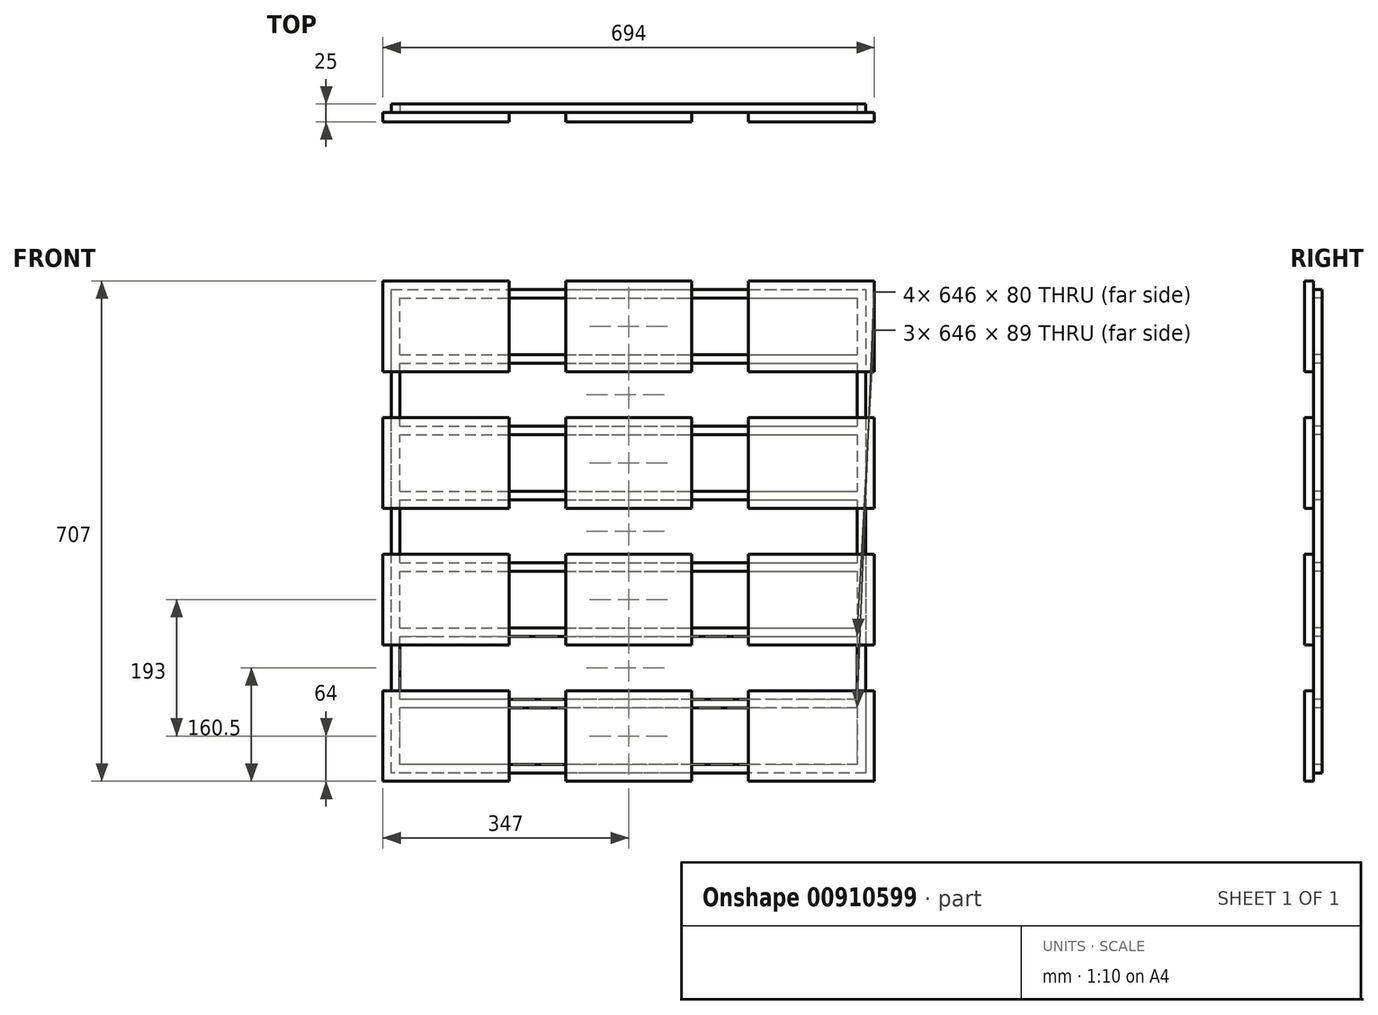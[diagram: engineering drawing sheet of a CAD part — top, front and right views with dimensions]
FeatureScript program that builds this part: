
annotation { "Feature Type Name" : "Feature", "Feature Type Description" : "" }
export const myFeature = defineFeature(function(context is Context, id is Id, definition is map)
    precondition{}
    {
        {
            var Q0;
            Q0=qCreatedBy(makeId("Front.planeOp"),FACE);
            var sketch = newSketch(context, id + "F0", { "sketchPlane" : qUnion([Q0])});
            skLineSegment(sketch, "E0", {"start": v(0, 0) * mm, "end": v(694, 0) * mm, "construction": true});
            skLineSegment(sketch, "E1", {"start": v(694, 0) * mm, "end": v(694, -707) * mm, "construction": true});
            skLineSegment(sketch, "E2", {"start": v(694, -707) * mm, "end": v(0, -707) * mm, "construction": true});
            skLineSegment(sketch, "E3", {"start": v(0, -707) * mm, "end": v(0, 0) * mm, "construction": true});
            skLineSegment(sketch, "E4.0", {"start": v(24, -24) * mm, "end": v(670, -24) * mm});
            skLineSegment(sketch, "E4.1", {"start": v(24, -683) * mm, "end": v(24, -603) * mm});
            skLineSegment(sketch, "E4.2", {"start": v(670, -683) * mm, "end": v(24, -683) * mm});
            skLineSegment(sketch, "E4.3", {"start": v(670, -24) * mm, "end": v(670, -104) * mm});
            skLineSegment(sketch, "E5", {"start": v(24, -116) * mm, "end": v(670, -116) * mm});
            skLineSegment(sketch, "E6", {"start": v(24, -205) * mm, "end": v(670, -205) * mm});
            skLineSegment(sketch, "E7", {"start": v(24, -309) * mm, "end": v(670, -309) * mm});
            skLineSegment(sketch, "E8", {"start": v(24, -398) * mm, "end": v(670, -398) * mm});
            skLineSegment(sketch, "E9.0", {"start": v(24, -104) * mm, "end": v(670, -104) * mm});
            skLineSegment(sketch, "E10.0", {"start": v(24, -217) * mm, "end": v(670, -217) * mm});
            skLineSegment(sketch, "E11.0", {"start": v(24, -410) * mm, "end": v(670, -410) * mm});
            skLineSegment(sketch, "E12.0", {"start": v(24, -297) * mm, "end": v(670, -297) * mm});
            skLineSegment(sketch, "E13.trimOffspring", {"start": v(670, -116) * mm, "end": v(670, -205) * mm});
            skLineSegment(sketch, "E14.trimOffspring", {"start": v(670, -217) * mm, "end": v(670, -297) * mm});
            skLineSegment(sketch, "E15.trimOffspring", {"start": v(670, -309) * mm, "end": v(670, -398) * mm});
            skLineSegment(sketch, "E16.trimOffspring", {"start": v(670, -410) * mm, "end": v(670, -490) * mm});
            skLineSegment(sketch, "E17.trimOffspring", {"start": v(24, -104) * mm, "end": v(24, -24) * mm});
            skLineSegment(sketch, "E18.trimOffspring", {"start": v(24, -205) * mm, "end": v(24, -116) * mm});
            skLineSegment(sketch, "E19.trimOffspring", {"start": v(24, -398) * mm, "end": v(24, -309) * mm});
            skLineSegment(sketch, "E20.trimOffspring", {"start": v(24, -297) * mm, "end": v(24, -217) * mm});
            skLineSegment(sketch, "E21.0", {"start": v(12, -695) * mm, "end": v(12, -12) * mm});
            skLineSegment(sketch, "E21.1", {"start": v(682, -695) * mm, "end": v(12, -695) * mm});
            skLineSegment(sketch, "E21.2", {"start": v(682, -12) * mm, "end": v(682, -695) * mm});
            skLineSegment(sketch, "E21.3", {"start": v(12, -12) * mm, "end": v(682, -12) * mm});
            skLineSegment(sketch, "E22", {"start": v(24, -490) * mm, "end": v(670, -490) * mm});
            skLineSegment(sketch, "E23", {"start": v(24, -502) * mm, "end": v(670, -502) * mm});
            skPoint(sketch, "E23.endSnap0", {"position": v(670, -546.5) * mm});
            skLineSegment(sketch, "E24", {"start": v(670, -591) * mm, "end": v(24, -591) * mm});
            skLineSegment(sketch, "E25", {"start": v(670, -603) * mm, "end": v(24, -603) * mm});
            skLineSegment(sketch, "E26.trimOffspring", {"start": v(24, -490) * mm, "end": v(24, -410) * mm});
            skLineSegment(sketch, "E27.trimOffspring", {"start": v(24, -591) * mm, "end": v(24, -502) * mm});
            skLineSegment(sketch, "E28.trimOffspring", {"start": v(670, -502) * mm, "end": v(670, -591) * mm});
            skLineSegment(sketch, "E29.trimOffspring", {"start": v(670, -603) * mm, "end": v(670, -683) * mm});
            skSolve(sketch);
        }
        {
            var Q0;
            Q0=makeQuery(id+"F0.imprint","IMPRINT",FACE,{"disambiguationData":[TD([[makeQuery(id+"F0.imprint","IMPRINT",EDGE,{"derivedFrom":sQuery(id+"F0.wireOp",EDGE,"E4.0")}),1.0]])]});
            extrude(context, id + "F1", {"entities" : qUnion([Q0]), "oppositeDirection" : true, "depth" : 12 * mm, "offsetDistance" : 25 * mm});
        }
        {
            var Q0;
            Q0=qCreatedBy(makeId("Front.planeOp"),FACE);
            var sketch = newSketch(context, id + "F2", { "sketchPlane" : qUnion([Q0])});
            skLineSegment(sketch, "E30.bottom", {"start": v(0, 0) * mm, "end": v(178, 0) * mm});
            skLineSegment(sketch, "E30.top", {"start": v(0, -128) * mm, "end": v(178, -128) * mm});
            skLineSegment(sketch, "E30.left", {"start": v(0, 0) * mm, "end": v(0, -128) * mm});
            skLineSegment(sketch, "E30.right", {"start": v(178, 0) * mm, "end": v(178, -128) * mm});
            skLineSegment(sketch, "E31.bottom", {"start": v(258, 0) * mm, "end": v(436, 0) * mm});
            skLineSegment(sketch, "E31.top", {"start": v(258, -128) * mm, "end": v(436, -128) * mm});
            skLineSegment(sketch, "E31.left", {"start": v(258, 0) * mm, "end": v(258, -128) * mm});
            skLineSegment(sketch, "E31.right", {"start": v(436, 0) * mm, "end": v(436, -128) * mm});
            skLineSegment(sketch, "E32.bottom", {"start": v(516, 0) * mm, "end": v(694, 0) * mm});
            skLineSegment(sketch, "E32.top", {"start": v(516, -128) * mm, "end": v(694, -128) * mm});
            skLineSegment(sketch, "E32.left", {"start": v(516, 0) * mm, "end": v(516, -128) * mm});
            skLineSegment(sketch, "E32.right", {"start": v(694, 0) * mm, "end": v(694, -128) * mm});
            skLineSegment(sketch, "E33.bottom", {"start": v(0, -193) * mm, "end": v(178, -193) * mm});
            skLineSegment(sketch, "E33.top", {"start": v(0, -321) * mm, "end": v(178, -321) * mm});
            skLineSegment(sketch, "E33.left", {"start": v(0, -193) * mm, "end": v(0, -321) * mm});
            skLineSegment(sketch, "E33.right", {"start": v(178, -193) * mm, "end": v(178, -321) * mm});
            skLineSegment(sketch, "E34.bottom", {"start": v(258, -193) * mm, "end": v(436, -193) * mm});
            skLineSegment(sketch, "E34.top", {"start": v(258, -321) * mm, "end": v(436, -321) * mm});
            skLineSegment(sketch, "E34.left", {"start": v(258, -193) * mm, "end": v(258, -321) * mm});
            skLineSegment(sketch, "E34.right", {"start": v(436, -193) * mm, "end": v(436, -321) * mm});
            skLineSegment(sketch, "E35.bottom", {"start": v(516, -193) * mm, "end": v(694, -193) * mm});
            skLineSegment(sketch, "E35.top", {"start": v(516, -321) * mm, "end": v(694, -321) * mm});
            skLineSegment(sketch, "E35.left", {"start": v(516, -193) * mm, "end": v(516, -321) * mm});
            skLineSegment(sketch, "E35.right", {"start": v(694, -193) * mm, "end": v(694, -321) * mm});
            skLineSegment(sketch, "E36.bottom", {"start": v(0, -386) * mm, "end": v(178, -386) * mm});
            skLineSegment(sketch, "E36.top", {"start": v(0, -514) * mm, "end": v(178, -514) * mm});
            skLineSegment(sketch, "E36.left", {"start": v(0, -386) * mm, "end": v(0, -514) * mm});
            skLineSegment(sketch, "E36.right", {"start": v(178, -386) * mm, "end": v(178, -514) * mm});
            skLineSegment(sketch, "E37.bottom", {"start": v(258, -386) * mm, "end": v(436, -386) * mm});
            skLineSegment(sketch, "E37.top", {"start": v(258, -514) * mm, "end": v(436, -514) * mm});
            skLineSegment(sketch, "E37.left", {"start": v(258, -386) * mm, "end": v(258, -514) * mm});
            skLineSegment(sketch, "E37.right", {"start": v(436, -386) * mm, "end": v(436, -514) * mm});
            skLineSegment(sketch, "E38.bottom", {"start": v(516, -386) * mm, "end": v(694, -386) * mm});
            skLineSegment(sketch, "E38.top", {"start": v(516, -514) * mm, "end": v(694, -514) * mm});
            skLineSegment(sketch, "E38.left", {"start": v(516, -386) * mm, "end": v(516, -514) * mm});
            skLineSegment(sketch, "E38.right", {"start": v(694, -386) * mm, "end": v(694, -514) * mm});
            skLineSegment(sketch, "E39", {"start": v(178, 0) * mm, "end": v(258, 0) * mm, "construction": true});
            skLineSegment(sketch, "E40", {"start": v(436, 0) * mm, "end": v(516, 0) * mm, "construction": true});
            skLineSegment(sketch, "E41", {"start": v(694, 0) * mm, "end": v(774, 0) * mm, "construction": true});
            skLineSegment(sketch, "E42", {"start": v(0, -128) * mm, "end": v(0, -193) * mm, "construction": true});
            skLineSegment(sketch, "E43", {"start": v(0, -321) * mm, "end": v(0, -386) * mm, "construction": true});
            skLineSegment(sketch, "E44.bottom", {"start": v(0, -579) * mm, "end": v(178, -579) * mm});
            skLineSegment(sketch, "E44.top", {"start": v(0, -707) * mm, "end": v(178, -707) * mm});
            skLineSegment(sketch, "E44.left", {"start": v(0, -579) * mm, "end": v(0, -707) * mm});
            skLineSegment(sketch, "E44.right", {"start": v(178, -579) * mm, "end": v(178, -707) * mm});
            skLineSegment(sketch, "E45.bottom", {"start": v(258, -579) * mm, "end": v(436, -579) * mm});
            skLineSegment(sketch, "E45.top", {"start": v(258, -707) * mm, "end": v(436, -707) * mm});
            skLineSegment(sketch, "E45.left", {"start": v(258, -579) * mm, "end": v(258, -707) * mm});
            skLineSegment(sketch, "E45.right", {"start": v(436, -579) * mm, "end": v(436, -707) * mm});
            skLineSegment(sketch, "E46.bottom", {"start": v(516, -579) * mm, "end": v(694, -579) * mm});
            skLineSegment(sketch, "E46.top", {"start": v(516, -707) * mm, "end": v(694, -707) * mm});
            skLineSegment(sketch, "E46.left", {"start": v(516, -579) * mm, "end": v(516, -707) * mm});
            skLineSegment(sketch, "E46.right", {"start": v(694, -579) * mm, "end": v(694, -707) * mm});
            skLineSegment(sketch, "E47", {"start": v(0, -514) * mm, "end": v(0, -579) * mm, "construction": true});
            skSolve(sketch);
        }
        {
            var Q0;
            Q0=qSketchRegion(id+"F2",true);
            extrude(context, id + "F3", {"entities" : qUnion([Q0]), "depth" : 13 * mm, "offsetDistance" : 25 * mm});
        }
    });
